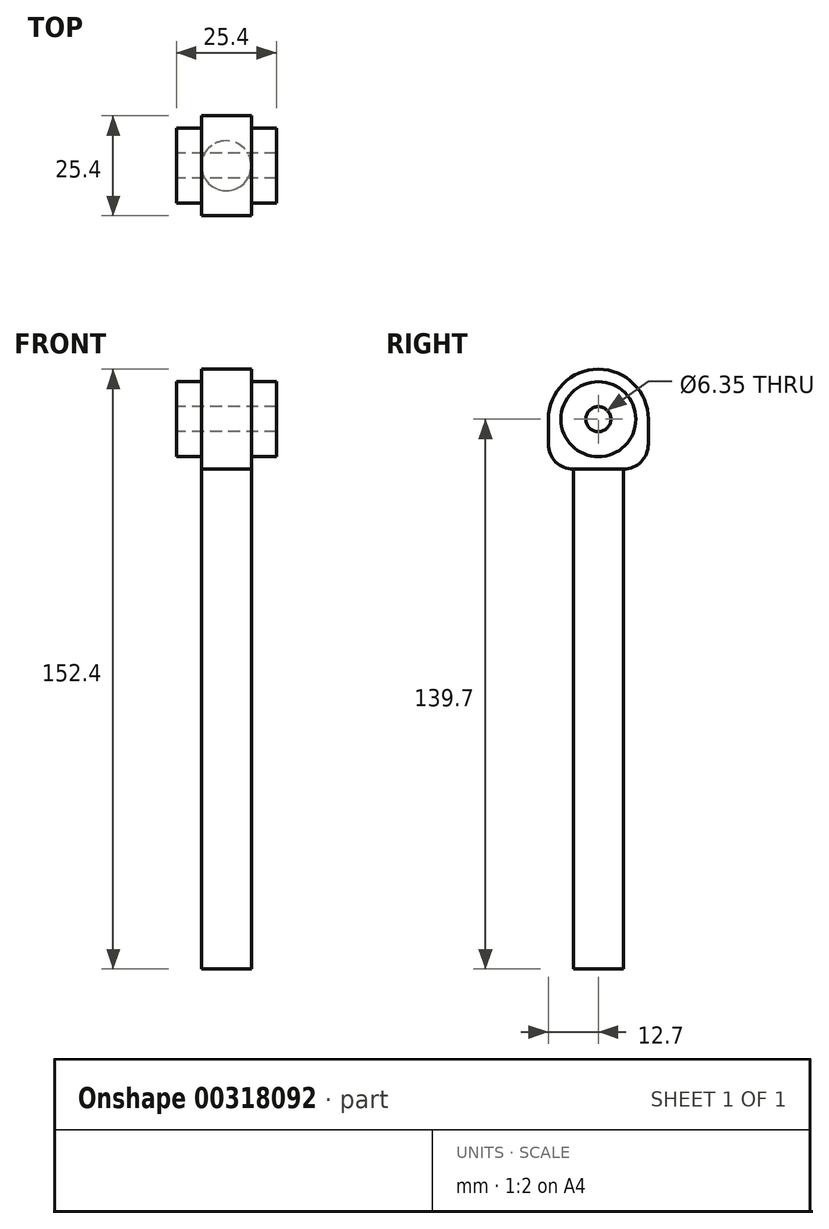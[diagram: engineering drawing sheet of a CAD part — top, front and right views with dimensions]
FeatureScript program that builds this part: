
annotation { "Feature Type Name" : "Feature", "Feature Type Description" : "" }
export const myFeature = defineFeature(function(context is Context, id is Id, definition is map)
    precondition{}
    {
        {
            var Q0;
            Q0=qCreatedBy(makeId("Top.planeOp"),FACE);
            var sketch = newSketch(context, id + "F0", { "sketchPlane" : qUnion([Q0])});
            skCircle(sketch, "E0", {"center": v(0, 0) * mm, "radius": 6.35 * mm});
            skSolve(sketch);
        }
        {
            var Q0;
            Q0 = qSketchRegion(id + "F0", true);
            extrude(context, id + "F1", {"entities" : qUnion([Q0]), "depth" : 127 * mm});
        }
        {
            var Q0;
            Q0=makeQuery(id+"F1.opExtrude","CAP_FACE",FACE,{"disambiguationData":[OSD([sQuery(id+"F0.wireOp",EDGE,"E0")])],"isStart":false});
            var sketch = newSketch(context, id + "F2", { "sketchPlane" : qUnion([Q0])});
            skLineSegment(sketch, "E1.bottom", {"start": v(-6.35, -12.7) * mm, "end": v(6.35, -12.7) * mm});
            skLineSegment(sketch, "E1.top", {"start": v(-6.35, 12.7) * mm, "end": v(6.35, 12.7) * mm});
            skLineSegment(sketch, "E1.left", {"start": v(-6.35, -12.7) * mm, "end": v(-6.35, 12.7) * mm});
            skLineSegment(sketch, "E1.right", {"start": v(6.35, -12.7) * mm, "end": v(6.35, 12.7) * mm});
            skPoint(sketch, "E1.middle", {"position": v(0, 0) * mm});
            skSolve(sketch);
        }
        {
            var Q0;
            Q0 = qSketchRegion(id + "F2", true);
            extrude(context, id + "F3", {"entities" : qUnion([Q0]), "operationType" : NewBodyOperationType.ADD, "depth" : 25.4 * mm});
        }
        {
            var Q0;
            Q0=makeQuery(id+"F3.opExtrude","SWEPT_FACE",FACE,{"disambiguationData":[OSD([sQuery(id+"F2.wireOp",EDGE,"E1.right")])]});
            var sketch = newSketch(context, id + "F4", { "sketchPlane" : qUnion([Q0])});
            skCircle(sketch, "E2", {"center": v(0, 139.7) * mm, "radius": 3.18 * mm});
            skCircle(sketch, "E3.0", {"center": v(0, 139.7) * mm, "radius": 9.52 * mm});
            skSolve(sketch);
        }
        {
            var Q0;
            Q0=makeQuery(id+"F4.imprint","IMPRINT",FACE,{"disambiguationData":[TD([[makeQuery(id+"F4.imprint","IMPRINT",EDGE,{"derivedFrom":sQuery(id+"F4.wireOp",EDGE,"E2")}),-1.0]])]});
            extrude(context, id + "F5", {"entities" : qUnion([Q0]), "operationType" : NewBodyOperationType.ADD, "depth" : 6.35 * mm, "hasSecondDirection" : true, "secondDirectionOppositeDirection" : true, "secondDirectionDepth" : 19.05 * mm});
        }
        {
            var Q0;
            Q0=makeQuery(id+"F5.boolean.opBoolean","SPLIT",FACE,{"disambiguationData":[TD([makeQuery(id+"F5.opExtrude","SWEPT_FACE",FACE,{"disambiguationData":[OSD([sQuery(id+"F4.wireOp",EDGE,"E2")])]})])],"derivedFrom":makeQuery(id+"F3.opExtrude","SWEPT_FACE",FACE,{"disambiguationData":[OSD([sQuery(id+"F2.wireOp",EDGE,"E1.right")])]})});
            extrude(context, id + "F6", {"entities" : qUnion([Q0]), "operationType" : NewBodyOperationType.REMOVE, "oppositeDirection" : true, "depth" : 25.4 * mm});
        }
        {
            var Q0;
            Q0=makeQuery(id+"F3.opExtrude","CAP_EDGE",EDGE,{"disambiguationData":[OSD([sQuery(id+"F2.wireOp",EDGE,"E1.bottom")])],"isStart":true});
            var Q1;
            Q1=makeQuery(id+"F3.opExtrude","CAP_EDGE",EDGE,{"disambiguationData":[OSD([sQuery(id+"F2.wireOp",EDGE,"E1.top")])],"isStart":true});
            fillet(context, id + "F7", {"entities" : qUnion([Q0, Q1]), "radius" : 6.35 * mm, "tangentPropagation" : true, "allowEdgeOverflow" : false});
        }
        {
            var Q0;
            Q0=makeQuery(id+"F3.opExtrude","CAP_EDGE",EDGE,{"disambiguationData":[OSD([sQuery(id+"F2.wireOp",EDGE,"E1.bottom")])],"isStart":false});
            var Q1;
            Q1=makeQuery(id+"F3.opExtrude","CAP_EDGE",EDGE,{"disambiguationData":[OSD([sQuery(id+"F2.wireOp",EDGE,"E1.top")])],"isStart":false});
            fillet(context, id + "F8", {"entities" : qUnion([Q0, Q1]), "radius" : 12.7 * mm, "tangentPropagation" : true, "allowEdgeOverflow" : false});
        }
    });
